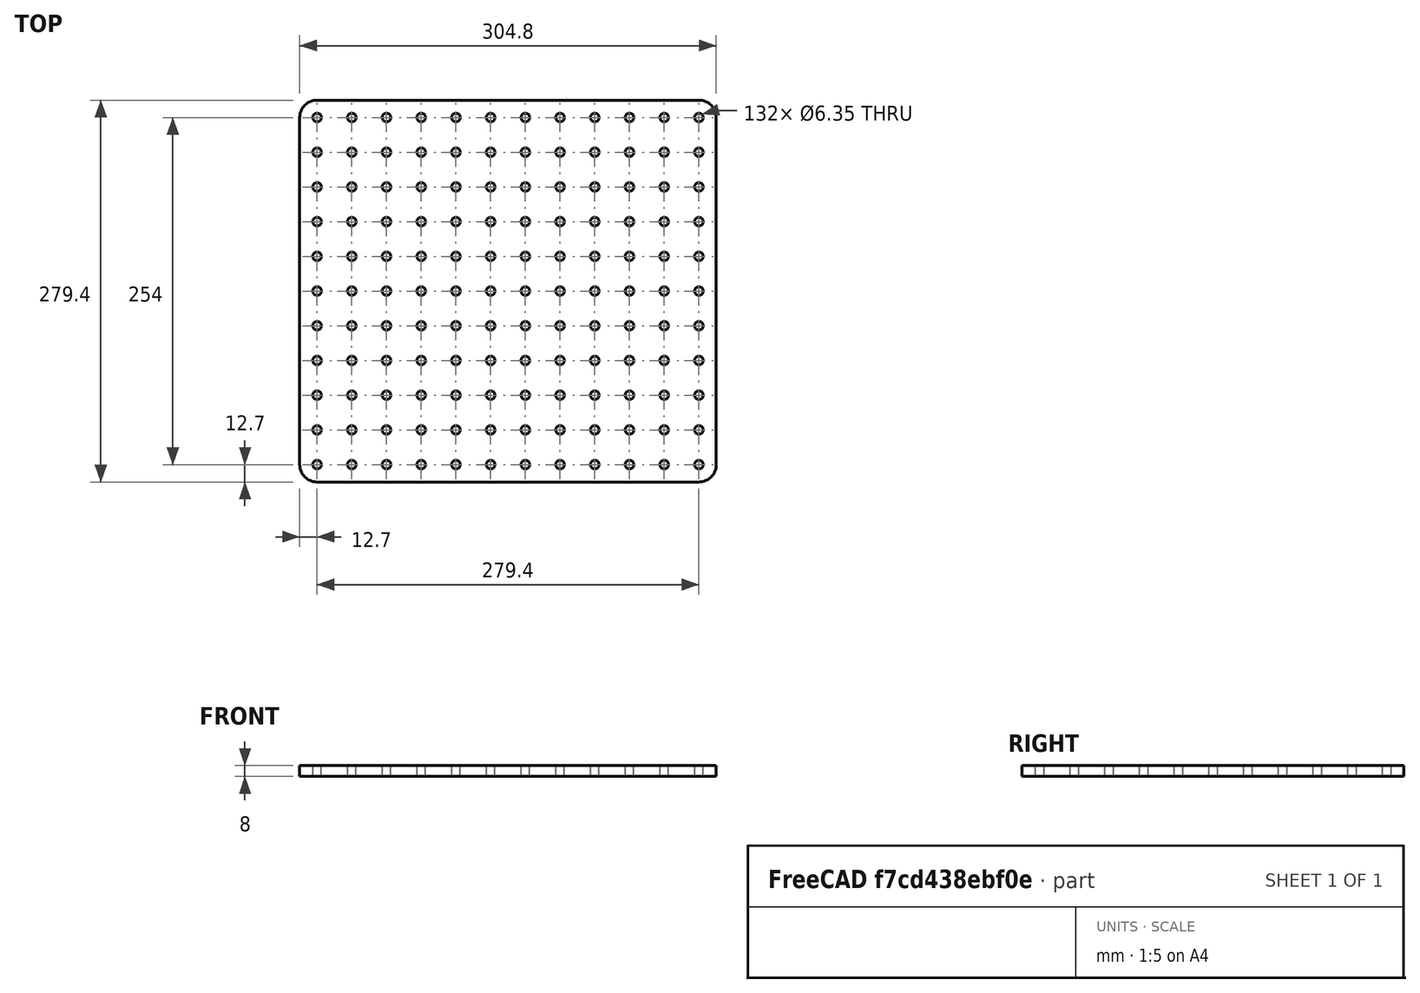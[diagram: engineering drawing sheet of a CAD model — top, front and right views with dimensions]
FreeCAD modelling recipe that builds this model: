
FCSTD DOCUMENT  (FreeCAD 0.19R24344 (Git))
Label: Baseplate
License: All rights reserved
LicenseURL: http://en.wikipedia.org/wiki/All_rights_reserved
objects: PartDesign::CoordinateSystem×13, Sketcher::SketchObject×1, PartDesign::Pad×1, PartDesign::Body×1
note: 17 computed .brp shape members not serialized (recipe doc carries the construction recipe); baked Part::Feature solids carry a one-line shape summary decoded from their .brp

FEATURE [Sketcher::SketchObject] Sketch
  FullyConstrained = true
  MapMode = 5
  Support = -> [XY_Plane]
  sketch-geometry (140):
    g0: LineSegment StartX=-139.7 StartY=139.7 StartZ=0 EndX=139.7 EndY=139.7 EndZ=0
    g1: LineSegment StartX=152.4 StartY=127 StartZ=0 EndX=152.4 EndY=-127 EndZ=0
    g2: LineSegment StartX=139.7 StartY=-139.7 StartZ=0 EndX=-139.7 EndY=-139.7 EndZ=0
    g3: LineSegment StartX=-152.4 StartY=-127 StartZ=0 EndX=-152.4 EndY=127 EndZ=0
    g4: ArcOfCircle CenterX=-139.7 CenterY=127 CenterZ=0 NormalX=0 NormalY=0 NormalZ=1 AngleXU=0 Radius=12.7 StartAngle=1.5708 EndAngle=3.14159
    g5: ArcOfCircle CenterX=-139.7 CenterY=-127 CenterZ=0 NormalX=0 NormalY=0 NormalZ=1 AngleXU=0 Radius=12.7 StartAngle=3.14159 EndAngle=4.71239
    g6: ArcOfCircle CenterX=139.7 CenterY=-127 CenterZ=0 NormalX=0 NormalY=0 NormalZ=1 AngleXU=0 Radius=12.7 StartAngle=4.71239 EndAngle=6.28319
    g7: ArcOfCircle CenterX=139.7 CenterY=127 CenterZ=0 NormalX=0 NormalY=0 NormalZ=1 AngleXU=0 Radius=12.7 StartAngle=2e-16 EndAngle=1.5708
    g8: Circle CenterX=-139.7 CenterY=127 CenterZ=0 NormalX=0 NormalY=0 NormalZ=1 AngleXU=0 Radius=3.175
    g9: Circle CenterX=-114.3 CenterY=127 CenterZ=0 NormalX=0 NormalY=0 NormalZ=1 AngleXU=0 Radius=3.175
    g10: Circle CenterX=-88.9 CenterY=127 CenterZ=0 NormalX=0 NormalY=0 NormalZ=1 AngleXU=0 Radius=3.175
    g11: Circle CenterX=-63.5 CenterY=127 CenterZ=0 NormalX=0 NormalY=0 NormalZ=1 AngleXU=0 Radius=3.175
    g12: Circle CenterX=-38.1 CenterY=127 CenterZ=0 NormalX=0 NormalY=0 NormalZ=1 AngleXU=0 Radius=3.175
    g13: Circle CenterX=-12.7 CenterY=127 CenterZ=0 NormalX=0 NormalY=0 NormalZ=1 AngleXU=0 Radius=3.175
    g14: Circle CenterX=12.7 CenterY=127 CenterZ=0 NormalX=0 NormalY=0 NormalZ=1 AngleXU=0 Radius=3.175
    g15: Circle CenterX=38.1 CenterY=127 CenterZ=0 NormalX=0 NormalY=0 NormalZ=1 AngleXU=0 Radius=3.175
    g16: Circle CenterX=63.5 CenterY=127 CenterZ=0 NormalX=0 NormalY=0 NormalZ=1 AngleXU=0 Radius=3.175
    g17: Circle CenterX=88.9 CenterY=127 CenterZ=0 NormalX=0 NormalY=0 NormalZ=1 AngleXU=0 Radius=3.175
    g18: Circle CenterX=114.3 CenterY=127 CenterZ=0 NormalX=0 NormalY=0 NormalZ=1 AngleXU=0 Radius=3.175
    g19: Circle CenterX=139.7 CenterY=127 CenterZ=0 NormalX=0 NormalY=0 NormalZ=1 AngleXU=0 Radius=3.175
    g20: Circle CenterX=-139.7 CenterY=101.6 CenterZ=0 NormalX=0 NormalY=0 NormalZ=1 AngleXU=0 Radius=3.175
    g21: Circle CenterX=-114.3 CenterY=101.6 CenterZ=0 NormalX=0 NormalY=0 NormalZ=1 AngleXU=0 Radius=3.175
    g22: Circle CenterX=-88.9 CenterY=101.6 CenterZ=0 NormalX=0 NormalY=0 NormalZ=1 AngleXU=0 Radius=3.175
    g23: Circle CenterX=-63.5 CenterY=101.6 CenterZ=0 NormalX=0 NormalY=0 NormalZ=1 AngleXU=0 Radius=3.175
    g24: Circle CenterX=-38.1 CenterY=101.6 CenterZ=0 NormalX=0 NormalY=0 NormalZ=1 AngleXU=0 Radius=3.175
    g25: Circle CenterX=-12.7 CenterY=101.6 CenterZ=0 NormalX=0 NormalY=0 NormalZ=1 AngleXU=0 Radius=3.175
    g26: Circle CenterX=12.7 CenterY=101.6 CenterZ=0 NormalX=0 NormalY=0 NormalZ=1 AngleXU=0 Radius=3.175
    g27: Circle CenterX=38.1 CenterY=101.6 CenterZ=0 NormalX=0 NormalY=0 NormalZ=1 AngleXU=0 Radius=3.175
    g28: Circle CenterX=63.5 CenterY=101.6 CenterZ=0 NormalX=0 NormalY=0 NormalZ=1 AngleXU=0 Radius=3.175
    g29: Circle CenterX=88.9 CenterY=101.6 CenterZ=0 NormalX=0 NormalY=0 NormalZ=1 AngleXU=0 Radius=3.175
    g30: Circle CenterX=114.3 CenterY=101.6 CenterZ=0 NormalX=0 NormalY=0 NormalZ=1 AngleXU=0 Radius=3.175
    g31: Circle CenterX=139.7 CenterY=101.6 CenterZ=0 NormalX=0 NormalY=0 NormalZ=1 AngleXU=0 Radius=3.175
    g32: Circle CenterX=-139.7 CenterY=76.2 CenterZ=0 NormalX=0 NormalY=0 NormalZ=1 AngleXU=0 Radius=3.175
    g33: Circle CenterX=-114.3 CenterY=76.2 CenterZ=0 NormalX=0 NormalY=0 NormalZ=1 AngleXU=0 Radius=3.175
    g34: Circle CenterX=-88.9 CenterY=76.2 CenterZ=0 NormalX=0 NormalY=0 NormalZ=1 AngleXU=0 Radius=3.175
    g35: Circle CenterX=-63.5 CenterY=76.2 CenterZ=0 NormalX=0 NormalY=0 NormalZ=1 AngleXU=0 Radius=3.175
    g36: Circle CenterX=-38.1 CenterY=76.2 CenterZ=0 NormalX=0 NormalY=0 NormalZ=1 AngleXU=0 Radius=3.175
    g37: Circle CenterX=-12.7 CenterY=76.2 CenterZ=0 NormalX=0 NormalY=0 NormalZ=1 AngleXU=0 Radius=3.175
    g38: Circle CenterX=12.7 CenterY=76.2 CenterZ=0 NormalX=0 NormalY=0 NormalZ=1 AngleXU=0 Radius=3.175
    g39: Circle CenterX=38.1 CenterY=76.2 CenterZ=0 NormalX=0 NormalY=0 NormalZ=1 AngleXU=0 Radius=3.175
    g40: Circle CenterX=63.5 CenterY=76.2 CenterZ=0 NormalX=0 NormalY=0 NormalZ=1 AngleXU=0 Radius=3.175
    g41: Circle CenterX=88.9 CenterY=76.2 CenterZ=0 NormalX=0 NormalY=0 NormalZ=1 AngleXU=0 Radius=3.175
    g42: Circle CenterX=114.3 CenterY=76.2 CenterZ=0 NormalX=0 NormalY=0 NormalZ=1 AngleXU=0 Radius=3.175
    g43: Circle CenterX=139.7 CenterY=76.2 CenterZ=0 NormalX=0 NormalY=0 NormalZ=1 AngleXU=0 Radius=3.175
    g44: Circle CenterX=-139.7 CenterY=50.8 CenterZ=0 NormalX=0 NormalY=0 NormalZ=1 AngleXU=0 Radius=3.175
    g45: Circle CenterX=-114.3 CenterY=50.8 CenterZ=0 NormalX=0 NormalY=0 NormalZ=1 AngleXU=0 Radius=3.175
    g46: Circle CenterX=-88.9 CenterY=50.8 CenterZ=0 NormalX=0 NormalY=0 NormalZ=1 AngleXU=0 Radius=3.175
    g47: Circle CenterX=-63.5 CenterY=50.8 CenterZ=0 NormalX=0 NormalY=0 NormalZ=1 AngleXU=0 Radius=3.175
    g48: Circle CenterX=-38.1 CenterY=50.8 CenterZ=0 NormalX=0 NormalY=0 NormalZ=1 AngleXU=0 Radius=3.175
    g49: Circle CenterX=-12.7 CenterY=50.8 CenterZ=0 NormalX=0 NormalY=0 NormalZ=1 AngleXU=0 Radius=3.175
    g50: Circle CenterX=12.7 CenterY=50.8 CenterZ=0 NormalX=0 NormalY=0 NormalZ=1 AngleXU=0 Radius=3.175
    g51: Circle CenterX=38.1 CenterY=50.8 CenterZ=0 NormalX=0 NormalY=0 NormalZ=1 AngleXU=0 Radius=3.175
    g52: Circle CenterX=63.5 CenterY=50.8 CenterZ=0 NormalX=0 NormalY=0 NormalZ=1 AngleXU=0 Radius=3.175
    g53: Circle CenterX=88.9 CenterY=50.8 CenterZ=0 NormalX=0 NormalY=0 NormalZ=1 AngleXU=0 Radius=3.175
    g54: Circle CenterX=114.3 CenterY=50.8 CenterZ=0 NormalX=0 NormalY=0 NormalZ=1 AngleXU=0 Radius=3.175
    g55: Circle CenterX=139.7 CenterY=50.8 CenterZ=0 NormalX=0 NormalY=0 NormalZ=1 AngleXU=0 Radius=3.175
    g56: Circle CenterX=-139.7 CenterY=25.4 CenterZ=0 NormalX=0 NormalY=0 NormalZ=1 AngleXU=0 Radius=3.175
    g57: Circle CenterX=-114.3 CenterY=25.4 CenterZ=0 NormalX=0 NormalY=0 NormalZ=1 AngleXU=0 Radius=3.175
    g58: Circle CenterX=-88.9 CenterY=25.4 CenterZ=0 NormalX=0 NormalY=0 NormalZ=1 AngleXU=0 Radius=3.175
    g59: Circle CenterX=-63.5 CenterY=25.4 CenterZ=0 NormalX=0 NormalY=0 NormalZ=1 AngleXU=0 Radius=3.175
    g60: Circle CenterX=-38.1 CenterY=25.4 CenterZ=0 NormalX=0 NormalY=0 NormalZ=1 AngleXU=0 Radius=3.175
    g61: Circle CenterX=-12.7 CenterY=25.4 CenterZ=0 NormalX=0 NormalY=0 NormalZ=1 AngleXU=0 Radius=3.175
    g62: Circle CenterX=12.7 CenterY=25.4 CenterZ=0 NormalX=0 NormalY=0 NormalZ=1 AngleXU=0 Radius=3.175
    g63: Circle CenterX=38.1 CenterY=25.4 CenterZ=0 NormalX=0 NormalY=0 NormalZ=1 AngleXU=0 Radius=3.175
    g64: Circle CenterX=63.5 CenterY=25.4 CenterZ=0 NormalX=0 NormalY=0 NormalZ=1 AngleXU=0 Radius=3.175
    g65: Circle CenterX=88.9 CenterY=25.4 CenterZ=0 NormalX=0 NormalY=0 NormalZ=1 AngleXU=0 Radius=3.175
    g66: Circle CenterX=114.3 CenterY=25.4 CenterZ=0 NormalX=0 NormalY=0 NormalZ=1 AngleXU=0 Radius=3.175
    g67: Circle CenterX=139.7 CenterY=25.4 CenterZ=0 NormalX=0 NormalY=0 NormalZ=1 AngleXU=0 Radius=3.175
    g68: Circle CenterX=-139.7 CenterY=8e-15 CenterZ=0 NormalX=0 NormalY=0 NormalZ=1 AngleXU=0 Radius=3.175
    g69: Circle CenterX=-114.3 CenterY=8e-15 CenterZ=0 NormalX=0 NormalY=0 NormalZ=1 AngleXU=0 Radius=3.175
    g70: Circle CenterX=-88.9 CenterY=8e-15 CenterZ=0 NormalX=0 NormalY=0 NormalZ=1 AngleXU=0 Radius=3.175
    g71: Circle CenterX=-63.5 CenterY=8e-15 CenterZ=0 NormalX=0 NormalY=0 NormalZ=1 AngleXU=0 Radius=3.175
    g72: Circle CenterX=-38.1 CenterY=8e-15 CenterZ=0 NormalX=0 NormalY=0 NormalZ=1 AngleXU=0 Radius=3.175
    g73: Circle CenterX=-12.7 CenterY=8e-15 CenterZ=0 NormalX=0 NormalY=0 NormalZ=1 AngleXU=0 Radius=3.175
    g74: Circle CenterX=12.7 CenterY=8e-15 CenterZ=0 NormalX=0 NormalY=0 NormalZ=1 AngleXU=0 Radius=3.175
    g75: Circle CenterX=38.1 CenterY=8e-15 CenterZ=0 NormalX=0 NormalY=0 NormalZ=1 AngleXU=0 Radius=3.175
    g76: Circle CenterX=63.5 CenterY=8e-15 CenterZ=0 NormalX=0 NormalY=0 NormalZ=1 AngleXU=0 Radius=3.175
    g77: Circle CenterX=88.9 CenterY=8e-15 CenterZ=0 NormalX=0 NormalY=0 NormalZ=1 AngleXU=0 Radius=3.175
    g78: Circle CenterX=114.3 CenterY=8e-15 CenterZ=0 NormalX=0 NormalY=0 NormalZ=1 AngleXU=0 Radius=3.175
    g79: Circle CenterX=139.7 CenterY=8e-15 CenterZ=0 NormalX=0 NormalY=0 NormalZ=1 AngleXU=0 Radius=3.175
    g80: Circle CenterX=-139.7 CenterY=-25.4 CenterZ=0 NormalX=0 NormalY=0 NormalZ=1 AngleXU=0 Radius=3.175
    g81: Circle CenterX=-114.3 CenterY=-25.4 CenterZ=0 NormalX=0 NormalY=0 NormalZ=1 AngleXU=0 Radius=3.175
    g82: Circle CenterX=-88.9 CenterY=-25.4 CenterZ=0 NormalX=0 NormalY=0 NormalZ=1 AngleXU=0 Radius=3.175
    g83: Circle CenterX=-63.5 CenterY=-25.4 CenterZ=0 NormalX=0 NormalY=0 NormalZ=1 AngleXU=0 Radius=3.175
    g84: Circle CenterX=-38.1 CenterY=-25.4 CenterZ=0 NormalX=0 NormalY=0 NormalZ=1 AngleXU=0 Radius=3.175
    g85: Circle CenterX=-12.7 CenterY=-25.4 CenterZ=0 NormalX=0 NormalY=0 NormalZ=1 AngleXU=0 Radius=3.175
    g86: Circle CenterX=12.7 CenterY=-25.4 CenterZ=0 NormalX=0 NormalY=0 NormalZ=1 AngleXU=0 Radius=3.175
    g87: Circle CenterX=38.1 CenterY=-25.4 CenterZ=0 NormalX=0 NormalY=0 NormalZ=1 AngleXU=0 Radius=3.175
    g88: Circle CenterX=63.5 CenterY=-25.4 CenterZ=0 NormalX=0 NormalY=0 NormalZ=1 AngleXU=0 Radius=3.175
    g89: Circle CenterX=88.9 CenterY=-25.4 CenterZ=0 NormalX=0 NormalY=0 NormalZ=1 AngleXU=0 Radius=3.175
    g90: Circle CenterX=114.3 CenterY=-25.4 CenterZ=0 NormalX=0 NormalY=0 NormalZ=1 AngleXU=0 Radius=3.175
    g91: Circle CenterX=139.7 CenterY=-25.4 CenterZ=0 NormalX=0 NormalY=0 NormalZ=1 AngleXU=0 Radius=3.175
    g92: Circle CenterX=-139.7 CenterY=-50.8 CenterZ=0 NormalX=0 NormalY=0 NormalZ=1 AngleXU=0 Radius=3.175
    g93: Circle CenterX=-114.3 CenterY=-50.8 CenterZ=0 NormalX=0 NormalY=0 NormalZ=1 AngleXU=0 Radius=3.175
    g94: Circle CenterX=-88.9 CenterY=-50.8 CenterZ=0 NormalX=0 NormalY=0 NormalZ=1 AngleXU=0 Radius=3.175
    g95: Circle CenterX=-63.5 CenterY=-50.8 CenterZ=0 NormalX=0 NormalY=0 NormalZ=1 AngleXU=0 Radius=3.175
    g96: Circle CenterX=-38.1 CenterY=-50.8 CenterZ=0 NormalX=0 NormalY=0 NormalZ=1 AngleXU=0 Radius=3.175
    g97: Circle CenterX=-12.7 CenterY=-50.8 CenterZ=0 NormalX=0 NormalY=0 NormalZ=1 AngleXU=0 Radius=3.175
    g98: Circle CenterX=12.7 CenterY=-50.8 CenterZ=0 NormalX=0 NormalY=0 NormalZ=1 AngleXU=0 Radius=3.175
    g99: Circle CenterX=38.1 CenterY=-50.8 CenterZ=0 NormalX=0 NormalY=0 NormalZ=1 AngleXU=0 Radius=3.175
    g100: Circle CenterX=63.5 CenterY=-50.8 CenterZ=0 NormalX=0 NormalY=0 NormalZ=1 AngleXU=0 Radius=3.175
    g101: Circle CenterX=88.9 CenterY=-50.8 CenterZ=0 NormalX=0 NormalY=0 NormalZ=1 AngleXU=0 Radius=3.175
    g102: Circle CenterX=114.3 CenterY=-50.8 CenterZ=0 NormalX=0 NormalY=0 NormalZ=1 AngleXU=0 Radius=3.175
    g103: Circle CenterX=139.7 CenterY=-50.8 CenterZ=0 NormalX=0 NormalY=0 NormalZ=1 AngleXU=0 Radius=3.175
    g104: Circle CenterX=-139.7 CenterY=-76.2 CenterZ=0 NormalX=0 NormalY=0 NormalZ=1 AngleXU=0 Radius=3.175
    g105: Circle CenterX=-114.3 CenterY=-76.2 CenterZ=0 NormalX=0 NormalY=0 NormalZ=1 AngleXU=0 Radius=3.175
    g106: Circle CenterX=-88.9 CenterY=-76.2 CenterZ=0 NormalX=0 NormalY=0 NormalZ=1 AngleXU=0 Radius=3.175
    g107: Circle CenterX=-63.5 CenterY=-76.2 CenterZ=0 NormalX=0 NormalY=0 NormalZ=1 AngleXU=0 Radius=3.175
    g108: Circle CenterX=-38.1 CenterY=-76.2 CenterZ=0 NormalX=0 NormalY=0 NormalZ=1 AngleXU=0 Radius=3.175
    g109: Circle CenterX=-12.7 CenterY=-76.2 CenterZ=0 NormalX=0 NormalY=0 NormalZ=1 AngleXU=0 Radius=3.175
    g110: Circle CenterX=12.7 CenterY=-76.2 CenterZ=0 NormalX=0 NormalY=0 NormalZ=1 AngleXU=0 Radius=3.175
    g111: Circle CenterX=38.1 CenterY=-76.2 CenterZ=0 NormalX=0 NormalY=0 NormalZ=1 AngleXU=0 Radius=3.175
    g112: Circle CenterX=63.5 CenterY=-76.2 CenterZ=0 NormalX=0 NormalY=0 NormalZ=1 AngleXU=0 Radius=3.175
    g113: Circle CenterX=88.9 CenterY=-76.2 CenterZ=0 NormalX=0 NormalY=0 NormalZ=1 AngleXU=0 Radius=3.175
    g114: Circle CenterX=114.3 CenterY=-76.2 CenterZ=0 NormalX=0 NormalY=0 NormalZ=1 AngleXU=0 Radius=3.175
    g115: Circle CenterX=139.7 CenterY=-76.2 CenterZ=0 NormalX=0 NormalY=0 NormalZ=1 AngleXU=0 Radius=3.175
    g116: Circle CenterX=-139.7 CenterY=-101.6 CenterZ=0 NormalX=0 NormalY=0 NormalZ=1 AngleXU=0 Radius=3.175
    g117: Circle CenterX=-114.3 CenterY=-101.6 CenterZ=0 NormalX=0 NormalY=0 NormalZ=1 AngleXU=0 Radius=3.175
    g118: Circle CenterX=-88.9 CenterY=-101.6 CenterZ=0 NormalX=0 NormalY=0 NormalZ=1 AngleXU=0 Radius=3.175
    g119: Circle CenterX=-63.5 CenterY=-101.6 CenterZ=0 NormalX=0 NormalY=0 NormalZ=1 AngleXU=0 Radius=3.175
    g120: Circle CenterX=-38.1 CenterY=-101.6 CenterZ=0 NormalX=0 NormalY=0 NormalZ=1 AngleXU=0 Radius=3.175
    g121: Circle CenterX=-12.7 CenterY=-101.6 CenterZ=0 NormalX=0 NormalY=0 NormalZ=1 AngleXU=0 Radius=3.175
    g122: Circle CenterX=12.7 CenterY=-101.6 CenterZ=0 NormalX=0 NormalY=0 NormalZ=1 AngleXU=0 Radius=3.175
    g123: Circle CenterX=38.1 CenterY=-101.6 CenterZ=0 NormalX=0 NormalY=0 NormalZ=1 AngleXU=0 Radius=3.175
    g124: Circle CenterX=63.5 CenterY=-101.6 CenterZ=0 NormalX=0 NormalY=0 NormalZ=1 AngleXU=0 Radius=3.175
    g125: Circle CenterX=88.9 CenterY=-101.6 CenterZ=0 NormalX=0 NormalY=0 NormalZ=1 AngleXU=0 Radius=3.175
    g126: Circle CenterX=114.3 CenterY=-101.6 CenterZ=0 NormalX=0 NormalY=0 NormalZ=1 AngleXU=0 Radius=3.175
    g127: Circle CenterX=139.7 CenterY=-101.6 CenterZ=0 NormalX=0 NormalY=0 NormalZ=1 AngleXU=0 Radius=3.175
    g128: Circle CenterX=-139.7 CenterY=-127 CenterZ=0 NormalX=0 NormalY=0 NormalZ=1 AngleXU=0 Radius=3.175
    g129: Circle CenterX=-114.3 CenterY=-127 CenterZ=0 NormalX=0 NormalY=0 NormalZ=1 AngleXU=0 Radius=3.175
    g130: Circle CenterX=-88.9 CenterY=-127 CenterZ=0 NormalX=0 NormalY=0 NormalZ=1 AngleXU=0 Radius=3.175
    g131: Circle CenterX=-63.5 CenterY=-127 CenterZ=0 NormalX=0 NormalY=0 NormalZ=1 AngleXU=0 Radius=3.175
    g132: Circle CenterX=-38.1 CenterY=-127 CenterZ=0 NormalX=0 NormalY=0 NormalZ=1 AngleXU=0 Radius=3.175
    g133: Circle CenterX=-12.7 CenterY=-127 CenterZ=0 NormalX=0 NormalY=0 NormalZ=1 AngleXU=0 Radius=3.175
    g134: Circle CenterX=12.7 CenterY=-127 CenterZ=0 NormalX=0 NormalY=0 NormalZ=1 AngleXU=0 Radius=3.175
    g135: Circle CenterX=38.1 CenterY=-127 CenterZ=0 NormalX=0 NormalY=0 NormalZ=1 AngleXU=0 Radius=3.175
    g136: Circle CenterX=63.5 CenterY=-127 CenterZ=0 NormalX=0 NormalY=0 NormalZ=1 AngleXU=0 Radius=3.175
    g137: Circle CenterX=88.9 CenterY=-127 CenterZ=0 NormalX=0 NormalY=0 NormalZ=1 AngleXU=0 Radius=3.175
    g138: Circle CenterX=114.3 CenterY=-127 CenterZ=0 NormalX=0 NormalY=0 NormalZ=1 AngleXU=0 Radius=3.175
    g139: Circle CenterX=139.7 CenterY=-127 CenterZ=0 NormalX=0 NormalY=0 NormalZ=1 AngleXU=0 Radius=3.175
  constraints (414):
    c: Horizontal(g2)
    c: Vertical(g1)
    c: Tangent(g3,g4) = 1.5708
    c: Tangent(g0,g4) = 1.5708
    c: Tangent(g3,g5) = 1.5708
    c: Tangent(g2,g5) = 1.5708
    c: Tangent(g2,g6) = 1.5708
    c: Tangent(g1,g6) = 1.5708
    c: Tangent(g0,g7) = 1.5708
    c: Tangent(g1,g7) = 1.5708
    c: Diameter(g8) = 6.35
    c: Equal(g8,g9) = 6.35
    c: DistanceX(g8,g9) = 25.4
    c: DistanceX(g9,g10) = 25.4
    c: DistanceX(g10,g11) = 25.4
    c: DistanceX(g11,g12) = 25.4
    c: DistanceX(g12,g13) = 25.4
    c: DistanceX(g13,g14) = 25.4
    c: DistanceX(g14,g15) = 25.4
    c: DistanceX(g15,g16) = 25.4
    c: DistanceX(g16,g17) = 25.4
    c: DistanceX(g17,g18) = 25.4
    c: DistanceX(g18,g19) = 25.4
    c: Radius(g4) = 12.7
    c: Vertical(g3)
    c: Equal(g4,g5)
    c: Equal(g4,g7)
    c: DistanceX(g3,g1) = 304.8
    c: DistanceY(g2,g0) = 279.4
    c: Symmetric(g3,g1,g-2)
    c: Symmetric(g0,g2,g-1)
    c: Horizontal(g8,g9)
    c: Horizontal(g9,g10)
    c: Horizontal(g10,g11)
    c: Horizontal(g12,g13)
    c: Horizontal(g13,g14)
    c: Horizontal(g14,g15)
    c: Horizontal(g15,g16)
    c: Horizontal(g16,g17)
    c: Horizontal(g17,g18)
    c: Horizontal(g18,g19)
    c: Horizontal(g12,g11)
    c: Equal(g9,g10)
    c: Equal(g10,g11)
    c: Equal(g11,g12)
    c: Equal(g12,g13)
    c: Equal(g13,g14)
    c: Equal(g14,g15)
    c: Equal(g15,g16)
    c: Equal(g16,g17)
    c: Equal(g17,g18)
    c: Equal(g18,g19)
    c: Equal(g8,g20) = 6.35
    c: Equal(g20,g21) = 6.35
    c: DistanceX(g20,g21) = 25.4
    c: DistanceX(g21,g22) = 25.4
    c: DistanceX(g22,g23) = 25.4
    c: DistanceX(g23,g24) = 25.4
    c: DistanceX(g24,g25) = 25.4
    c: DistanceX(g25,g26) = 25.4
    c: DistanceX(g26,g27) = 25.4
    c: DistanceX(g27,g28) = 25.4
    c: DistanceX(g28,g29) = 25.4
    c: DistanceX(g29,g30) = 25.4
    c: DistanceX(g30,g31) = 25.4
    c: Horizontal(g20,g21)
    c: Horizontal(g21,g22)
    c: Horizontal(g22,g23)
    c: Horizontal(g24,g25)
    c: Horizontal(g25,g26)
    c: Horizontal(g26,g27)
    c: Horizontal(g27,g28)
    c: Horizontal(g28,g29)
    c: Horizontal(g29,g30)
    c: Horizontal(g30,g31)
    c: Horizontal(g24,g23)
    c: Equal(g21,g22)
    c: Equal(g22,g23)
    c: Equal(g23,g24)
    c: Equal(g24,g25)
    c: Equal(g25,g26)
    c: Equal(g26,g27)
    c: Equal(g27,g28)
    c: Equal(g28,g29)
    c: Equal(g29,g30)
    c: Equal(g30,g31)
    c: DistanceY(g20,g8) = 25.4
    c: Vertical(g20,g8)
    c: Equal(g8,g32) = 6.35
    c: Equal(g32,g33) = 6.35
    c: DistanceX(g32,g33) = 25.4
    c: DistanceX(g33,g34) = 25.4
    c: DistanceX(g34,g35) = 25.4
    c: DistanceX(g35,g36) = 25.4
    c: DistanceX(g36,g37) = 25.4
    c: DistanceX(g37,g38) = 25.4
    c: DistanceX(g38,g39) = 25.4
    c: DistanceX(g39,g40) = 25.4
    c: DistanceX(g40,g41) = 25.4
    c: DistanceX(g41,g42) = 25.4
    c: DistanceX(g42,g43) = 25.4
    c: Horizontal(g32,g33)
    c: Horizontal(g33,g34)
    c: Horizontal(g34,g35)
    c: Horizontal(g36,g37)
    c: Horizontal(g37,g38)
    c: Horizontal(g38,g39)
    c: Horizontal(g39,g40)
    c: Horizontal(g40,g41)
    c: Horizontal(g41,g42)
    c: Horizontal(g42,g43)
    c: Horizontal(g36,g35)
    c: Equal(g33,g34)
    c: Equal(g34,g35)
    c: Equal(g35,g36)
    c: Equal(g36,g37)
    c: Equal(g37,g38)
    c: Equal(g38,g39)
    c: Equal(g39,g40)
    c: Equal(g40,g41)
    c: Equal(g41,g42)
    c: Equal(g42,g43)
    c: Equal(g32,g44) = 6.35
    c: Equal(g44,g45) = 6.35
    c: DistanceX(g44,g45) = 25.4
    c: DistanceX(g45,g46) = 25.4
    c: DistanceX(g46,g47) = 25.4
    c: DistanceX(g47,g48) = 25.4
    c: DistanceX(g48,g49) = 25.4
    c: DistanceX(g49,g50) = 25.4
    c: DistanceX(g50,g51) = 25.4
    c: DistanceX(g51,g52) = 25.4
    c: DistanceX(g52,g53) = 25.4
    c: DistanceX(g53,g54) = 25.4
    c: DistanceX(g54,g55) = 25.4
    c: Horizontal(g44,g45)
    c: Horizontal(g45,g46)
    c: Horizontal(g46,g47)
    c: Horizontal(g48,g49)
    c: Horizontal(g49,g50)
    c: Horizontal(g50,g51)
    c: Horizontal(g51,g52)
    c: Horizontal(g52,g53)
    c: Horizontal(g53,g54)
    c: Horizontal(g54,g55)
    c: Horizontal(g48,g47)
    c: Equal(g45,g46)
    c: Equal(g46,g47)
    c: Equal(g47,g48)
    c: Equal(g48,g49)
    c: Equal(g49,g50)
    c: Equal(g50,g51)
    c: Equal(g51,g52)
    c: Equal(g52,g53)
    c: Equal(g53,g54)
    c: Equal(g54,g55)
    c: DistanceY(g44,g32) = 25.4
    c: Vertical(g44,g32)
    c: Vertical(g32,g20)
    c: DistanceY(g32,g20) = 25.4
    c: Equal(g8,g56) = 6.35
    c: Equal(g56,g57) = 6.35
    c: DistanceX(g56,g57) = 25.4
    c: DistanceX(g57,g58) = 25.4
    c: DistanceX(g58,g59) = 25.4
    c: DistanceX(g59,g60) = 25.4
    c: DistanceX(g60,g61) = 25.4
    c: DistanceX(g61,g62) = 25.4
    c: DistanceX(g62,g63) = 25.4
    c: DistanceX(g63,g64) = 25.4
    c: DistanceX(g64,g65) = 25.4
    c: DistanceX(g65,g66) = 25.4
    c: DistanceX(g66,g67) = 25.4
    c: Horizontal(g56,g57)
    c: Horizontal(g57,g58)
    c: Horizontal(g58,g59)
    c: Horizontal(g60,g61)
    c: Horizontal(g61,g62)
    c: Horizontal(g62,g63)
    c: Horizontal(g63,g64)
    c: Horizontal(g64,g65)
    c: Horizontal(g65,g66)
    c: Horizontal(g66,g67)
    c: Horizontal(g60,g59)
    c: Equal(g57,g58)
    c: Equal(g58,g59)
    c: Equal(g59,g60)
    c: Equal(g60,g61)
    c: Equal(g61,g62)
    c: Equal(g62,g63)
    c: Equal(g63,g64)
    c: Equal(g64,g65)
    c: Equal(g65,g66)
    c: Equal(g66,g67)
    c: Equal(g56,g68) = 6.35
    c: Equal(g68,g69) = 6.35
    c: DistanceX(g68,g69) = 25.4
    c: DistanceX(g69,g70) = 25.4
    c: DistanceX(g70,g71) = 25.4
    c: DistanceX(g71,g72) = 25.4
    c: DistanceX(g72,g73) = 25.4
    c: DistanceX(g73,g74) = 25.4
    c: DistanceX(g74,g75) = 25.4
    c: DistanceX(g75,g76) = 25.4
    c: DistanceX(g76,g77) = 25.4
    c: DistanceX(g77,g78) = 25.4
    c: DistanceX(g78,g79) = 25.4
    c: Horizontal(g68,g69)
    c: Horizontal(g69,g70)
    c: Horizontal(g70,g71)
    c: Horizontal(g72,g73)
    c: Horizontal(g73,g74)
    c: Horizontal(g74,g75)
    c: Horizontal(g75,g76)
    c: Horizontal(g76,g77)
    c: Horizontal(g77,g78)
    c: Horizontal(g78,g79)
    c: Horizontal(g72,g71)
    c: Equal(g69,g70)
    c: Equal(g70,g71)
    c: Equal(g71,g72)
    c: Equal(g72,g73)
    c: Equal(g73,g74)
    c: Equal(g74,g75)
    c: Equal(g75,g76)
    c: Equal(g76,g77)
    c: Equal(g77,g78)
    c: Equal(g78,g79)
    c: DistanceY(g68,g56) = 25.4
    c: Vertical(g68,g56)
    c: Equal(g56,g80) = 6.35
    c: Equal(g80,g81) = 6.35
    c: DistanceX(g80,g81) = 25.4
    c: DistanceX(g81,g82) = 25.4
    c: DistanceX(g82,g83) = 25.4
    c: DistanceX(g83,g84) = 25.4
    c: DistanceX(g84,g85) = 25.4
    c: DistanceX(g85,g86) = 25.4
    c: DistanceX(g86,g87) = 25.4
    c: DistanceX(g87,g88) = 25.4
    c: DistanceX(g88,g89) = 25.4
    c: DistanceX(g89,g90) = 25.4
    c: DistanceX(g90,g91) = 25.4
    c: Horizontal(g80,g81)
    c: Horizontal(g81,g82)
    c: Horizontal(g82,g83)
    c: Horizontal(g84,g85)
    c: Horizontal(g85,g86)
    c: Horizontal(g86,g87)
    c: Horizontal(g87,g88)
    c: Horizontal(g88,g89)
    c: Horizontal(g89,g90)
    c: Horizontal(g90,g91)
    c: Horizontal(g84,g83)
    c: Equal(g81,g82)
    c: Equal(g82,g83)
    c: Equal(g83,g84)
    c: Equal(g84,g85)
    c: Equal(g85,g86)
    c: Equal(g86,g87)
    c: Equal(g87,g88)
    c: Equal(g88,g89)
    c: Equal(g89,g90)
    c: Equal(g90,g91)
    c: Equal(g80,g92) = 6.35
    c: Equal(g92,g93) = 6.35
    c: DistanceX(g92,g93) = 25.4
    c: DistanceX(g93,g94) = 25.4
    c: DistanceX(g94,g95) = 25.4
    c: DistanceX(g95,g96) = 25.4
    c: DistanceX(g96,g97) = 25.4
    c: DistanceX(g97,g98) = 25.4
    c: DistanceX(g98,g99) = 25.4
    c: DistanceX(g99,g100) = 25.4
    c: DistanceX(g100,g101) = 25.4
    c: DistanceX(g101,g102) = 25.4
    c: DistanceX(g102,g103) = 25.4
    c: Horizontal(g92,g93)
    c: Horizontal(g93,g94)
    c: Horizontal(g94,g95)
    c: Horizontal(g96,g97)
    c: Horizontal(g97,g98)
    c: Horizontal(g98,g99)
    c: Horizontal(g99,g100)
    c: Horizontal(g100,g101)
    c: Horizontal(g101,g102)
    c: Horizontal(g102,g103)
    c: Horizontal(g96,g95)
    c: Equal(g93,g94)
    c: Equal(g94,g95)
    c: Equal(g95,g96)
    c: Equal(g96,g97)
    c: Equal(g97,g98)
    c: Equal(g98,g99)
    c: Equal(g99,g100)
    c: Equal(g100,g101)
    c: Equal(g101,g102)
    c: Equal(g102,g103)
    c: DistanceY(g92,g80) = 25.4
    c: Vertical(g92,g80)
    c: Vertical(g80,g68)
    c: DistanceY(g80,g68) = 25.4
    c: DistanceY(g56,g44) = 25.4
    c: Vertical(g56,g44)
    c: Equal(g104,g105) = 6.35
    c: DistanceX(g104,g105) = 25.4
    c: DistanceX(g105,g106) = 25.4
    c: DistanceX(g106,g107) = 25.4
    c: DistanceX(g107,g108) = 25.4
    c: DistanceX(g108,g109) = 25.4
    c: DistanceX(g109,g110) = 25.4
    c: DistanceX(g110,g111) = 25.4
    c: DistanceX(g111,g112) = 25.4
    c: DistanceX(g112,g113) = 25.4
    c: DistanceX(g113,g114) = 25.4
    c: DistanceX(g114,g115) = 25.4
    c: Horizontal(g104,g105)
    c: Horizontal(g105,g106)
    c: Horizontal(g106,g107)
    c: Horizontal(g108,g109)
    c: Horizontal(g109,g110)
    c: Horizontal(g110,g111)
    c: Horizontal(g111,g112)
    c: Horizontal(g112,g113)
    c: Horizontal(g113,g114)
    c: Horizontal(g114,g115)
    c: Horizontal(g108,g107)
    c: Equal(g105,g106)
    c: Equal(g106,g107)
    c: Equal(g107,g108)
    c: Equal(g108,g109)
    c: Equal(g109,g110)
    c: Equal(g110,g111)
    c: Equal(g111,g112)
    c: Equal(g112,g113)
    c: Equal(g113,g114)
    c: Equal(g114,g115)
    c: Equal(g116,g117) = 6.35
    c: DistanceX(g116,g117) = 25.4
    c: DistanceX(g117,g118) = 25.4
    c: DistanceX(g118,g119) = 25.4
    c: DistanceX(g119,g120) = 25.4
    c: DistanceX(g120,g121) = 25.4
    c: DistanceX(g121,g122) = 25.4
    c: DistanceX(g122,g123) = 25.4
    c: DistanceX(g123,g124) = 25.4
    c: DistanceX(g124,g125) = 25.4
    c: DistanceX(g125,g126) = 25.4
    c: DistanceX(g126,g127) = 25.4
    c: Horizontal(g116,g117)
    c: Horizontal(g117,g118)
    c: Horizontal(g118,g119)
    c: Horizontal(g120,g121)
    c: Horizontal(g121,g122)
    c: Horizontal(g122,g123)
    c: Horizontal(g123,g124)
    c: Horizontal(g124,g125)
    c: Horizontal(g125,g126)
    c: Horizontal(g126,g127)
    c: Horizontal(g120,g119)
    c: Equal(g117,g118)
    c: Equal(g118,g119)
    c: Equal(g119,g120)
    c: Equal(g120,g121)
    c: Equal(g121,g122)
    c: Equal(g122,g123)
    c: Equal(g123,g124)
    c: Equal(g124,g125)
    c: Equal(g125,g126)
    c: Equal(g126,g127)
    c: Equal(g116,g128) = 6.35
    c: Equal(g128,g129) = 6.35
    c: DistanceX(g128,g129) = 25.4
    c: DistanceX(g129,g130) = 25.4
    c: DistanceX(g130,g131) = 25.4
    c: DistanceX(g131,g132) = 25.4
    c: DistanceX(g132,g133) = 25.4
    c: DistanceX(g133,g134) = 25.4
    c: DistanceX(g134,g135) = 25.4
    c: DistanceX(g135,g136) = 25.4
    c: DistanceX(g136,g137) = 25.4
    c: DistanceX(g137,g138) = 25.4
    c: DistanceX(g138,g139) = 25.4
    c: Horizontal(g128,g129)
    c: Horizontal(g129,g130)
    c: Horizontal(g130,g131)
    c: Horizontal(g132,g133)
    c: Horizontal(g133,g134)
    c: Horizontal(g134,g135)
    c: Horizontal(g135,g136)
    c: Horizontal(g136,g137)
    c: Horizontal(g137,g138)
    c: Horizontal(g138,g139)
    c: Horizontal(g132,g131)
    c: Equal(g129,g130)
    c: Equal(g130,g131)
    c: Equal(g131,g132)
    c: Equal(g132,g133)
    c: Equal(g133,g134)
    c: Equal(g134,g135)
    c: Equal(g135,g136)
    c: Equal(g136,g137)
    c: Equal(g137,g138)
    c: Equal(g138,g139)
    c: DistanceY(g128,g116) = 25.4
    c: Vertical(g128,g116)
    c: Vertical(g116,g104)
    c: DistanceY(g116,g104) = 25.4
    c: Equal(g104,g92)
    c: DistanceY(g104,g92) = 25.4
    c: Vertical(g104,g92)
    c: Vertical(g128,g2)
    c: Horizontal(g128,g3)
    c: Equal(g116,g104)
FEATURE [PartDesign::Pad] Pad
  Direction = (1,1,1)
  Length = 8
  Length2 = 100
  Profile = -> Sketch
  Type = 0
FEATURE [PartDesign::CoordinateSystem] LCS_Edge
  AttacherType = Attacher::AttachEngine3D
  MapMode = 45
  Placement = pos=(-139.7,-127,8) rot=(0,0,-1;8.2e-05rad)
  Support = -> [Pad]
FEATURE [PartDesign::CoordinateSystem] LCS_Camera_Stand
  AttacherType = Attacher::AttachEngine3D
  MapMode = 45
  Placement = pos=(-88.9,-25.4,8) rot=(0,0,1;2.1e-05rad)
  Support = -> [Pad]
FEATURE [PartDesign::CoordinateSystem] LCS_Table_Foot1
  AttacherType = Attacher::AttachEngine3D
  MapMode = 45
  Placement = pos=(12.7,-25.4,8) rot=(0,0,-1;1e-06rad)
  Support = -> [Pad]
FEATURE [PartDesign::CoordinateSystem] LCS_Foot2
  AttacherType = Attacher::AttachEngine3D
  MapMode = 11
  Placement = pos=(12.7,25.4,8) rot=(0,0,1;1.5708rad)
  Support = -> [Pad]
FEATURE [PartDesign::CoordinateSystem] LCS_Foot3
  AttacherType = Attacher::AttachEngine3D
  MapMode = 11
  Placement = pos=(63.5,25.4,8) rot=(0,0,1;1.5708rad)
  Support = -> [Pad]
FEATURE [PartDesign::CoordinateSystem] LCS_Foot4
  AttacherType = Attacher::AttachEngine3D
  MapMode = 11
  Placement = pos=(63.5,-25.4,8) rot=(0,0,1;1.5708rad)
  Support = -> [Pad]
FEATURE [PartDesign::CoordinateSystem] LCS_Light1
  AttacherType = Attacher::AttachEngine3D
  MapMode = 11
  Placement = pos=(-38.1,-25.4,8) rot=(0,0,1;1.5708rad)
  Support = -> [Pad]
FEATURE [PartDesign::CoordinateSystem] LCS_Light2
  AttacherType = Attacher::AttachEngine3D
  MapMode = 11
  Placement = pos=(-38.1,25.4,8) rot=(0,0,1;1.5708rad)
  Support = -> [Pad]
FEATURE [PartDesign::CoordinateSystem] LCS_Light3
  AttacherType = Attacher::AttachEngine3D
  MapMode = 11
  Placement = pos=(-12.7,50.8,8) rot=(0,0,1;1.5708rad)
  Support = -> [Pad]
FEATURE [PartDesign::CoordinateSystem] LCS_Tablet
  AttacherType = Attacher::AttachEngine3D
FEATURE [PartDesign::CoordinateSystem] LCS_Tablet001
  AttacherType = Attacher::AttachEngine3D
  MapMode = 11
  Placement = pos=(114.3,25.4,8) rot=(0,0,1;1.5708rad)
  Support = -> [Pad]
FEATURE [PartDesign::CoordinateSystem] LCS_Micro
  AttacherType = Attacher::AttachEngine3D
  MapMode = 11
  Placement = pos=(12.7,-76.2,8) rot=(0,0,1;1.5708rad)
  Support = -> [Pad]
FEATURE [PartDesign::CoordinateSystem] LCS_Heat
  AttacherType = Attacher::AttachEngine3D
  MapMode = 11
  Placement = pos=(38.1,8e-15,8) rot=(0,0,1;1.5708rad)
  Support = -> [Pad]
FEATURE [PartDesign::Body] Body  label="Baseplate"
  Group = -> [Sketch,Pad,LCS_Edge,LCS_Camera_Stand,LCS_Table_Foot1,LCS_Foot2,LCS_Foot3,LCS_Foot4,LCS_Light1,LCS_Light2,LCS_Light3,LCS_Tablet,LCS_Tablet001,LCS_Micro,LCS_Heat]
  Origin = -> Origin
  Tip = -> Pad
